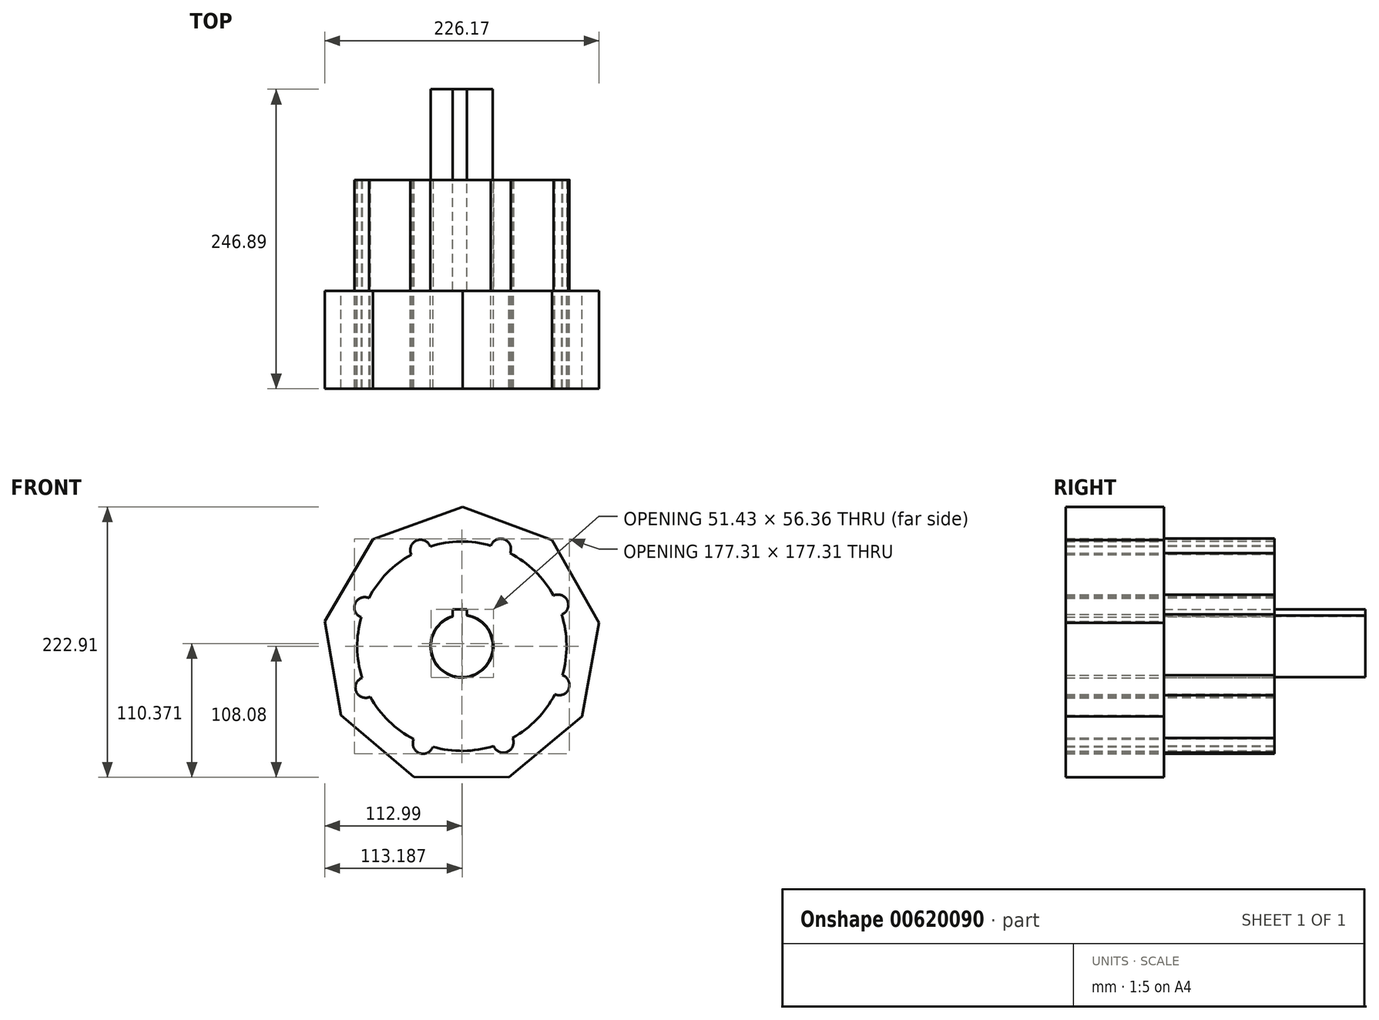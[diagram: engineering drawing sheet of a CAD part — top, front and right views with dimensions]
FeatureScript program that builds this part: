
annotation { "Feature Type Name" : "Feature", "Feature Type Description" : "" }
export const myFeature = defineFeature(function(context is Context, id is Id, definition is map)
    precondition{}
    {
        {
            var Q0;
            Q0=qCreatedBy(makeId("Front.planeOp"),FACE);
            var sketch = newSketch(context, id + "F0", { "sketchPlane" : qUnion([Q0])});
            skCircle(sketch, "E0.cCircle", {"center": v(-20.28, 0) * mm, "radius": 107.9 * mm, "construction": true});
            skLineSegment(sketch, "E0.0", {"start": v(92.9, 19.42) * mm, "end": v(78.9, -57.87) * mm});
            skLineSegment(sketch, "E0.1", {"start": v(78.9, -57.87) * mm, "end": v(18.5, -108.08) * mm});
            skLineSegment(sketch, "E0.2", {"start": v(18.5, -108.08) * mm, "end": v(-60.05, -107.72) * mm});
            skLineSegment(sketch, "E0.3", {"start": v(-60.05, -107.72) * mm, "end": v(-119.99, -56.96) * mm});
            skLineSegment(sketch, "E0.4", {"start": v(-119.99, -56.96) * mm, "end": v(-133.27, 20.46) * mm});
            skLineSegment(sketch, "E0.5", {"start": v(-133.27, 20.46) * mm, "end": v(-93.69, 88.3) * mm});
            skLineSegment(sketch, "E0.6", {"start": v(-93.69, 88.3) * mm, "end": v(-19.75, 114.83) * mm});
            skLineSegment(sketch, "E0.7", {"start": v(-19.75, 114.83) * mm, "end": v(53.93, 87.63) * mm});
            skLineSegment(sketch, "E0.8", {"start": v(53.93, 87.63) * mm, "end": v(92.9, 19.42) * mm});
            skPoint(sketch, "E0.0.midPoint", {"position": v(85.9, -19.22) * mm});
            skArc(sketch, "E1", {"start": v(-61.99, 75.56) * mm, "mid": v(-82.1, 60.21) * mm, "end": v(-96.91, 39.7) * mm});
            skArc(sketch, "E2", {"start": v(19.42, 76.63) * mm, "mid": v(14.84, 88.06) * mm, "end": v(3.65, 82.92) * mm});
            skArc(sketch, "E3.1.0", {"start": v(-46.4, 82.26) * mm, "mid": v(-57.71, 87.1) * mm, "end": v(-61.99, 75.56) * mm});
            skArc(sketch, "E3.2.0", {"start": v(-96.91, 39.7) * mm, "mid": v(-108.33, 35.12) * mm, "end": v(-103.2, 23.93) * mm});
            skArc(sketch, "E3.3.0", {"start": v(-102.54, -26.12) * mm, "mid": v(-107.38, -37.43) * mm, "end": v(-95.84, -41.7) * mm});
            skArc(sketch, "E3.4.0", {"start": v(-59.98, -76.63) * mm, "mid": v(-55.4, -88.06) * mm, "end": v(-44.21, -82.92) * mm});
            skArc(sketch, "E3.5.0", {"start": v(5.84, -82.26) * mm, "mid": v(17.15, -87.1) * mm, "end": v(21.43, -75.56) * mm});
            skArc(sketch, "E3.6.0", {"start": v(56.35, -39.7) * mm, "mid": v(67.78, -35.12) * mm, "end": v(62.64, -23.93) * mm});
            skArc(sketch, "E3.7.0", {"start": v(61.98, 26.12) * mm, "mid": v(66.82, 37.43) * mm, "end": v(55.28, 41.7) * mm});
            skArc(sketch, "E4.trimOffspring", {"start": v(-103.2, 23.93) * mm, "mid": v(-106.58, -1.14) * mm, "end": v(-102.54, -26.12) * mm});
            skArc(sketch, "E5.trimOffspring", {"start": v(-95.84, -41.7) * mm, "mid": v(-80.5, -61.83) * mm, "end": v(-59.98, -76.63) * mm});
            skArc(sketch, "E6.trimOffspring", {"start": v(-44.21, -82.92) * mm, "mid": v(-19.14, -86.3) * mm, "end": v(5.84, -82.26) * mm});
            skArc(sketch, "E7.trimOffspring", {"start": v(3.65, 82.92) * mm, "mid": v(-21.42, 86.3) * mm, "end": v(-46.4, 82.26) * mm});
            skArc(sketch, "E8.trimOffspring", {"start": v(21.43, -75.56) * mm, "mid": v(41.55, -60.21) * mm, "end": v(56.35, -39.7) * mm});
            skArc(sketch, "E9.trimOffspring", {"start": v(62.64, -23.93) * mm, "mid": v(66.02, 1.14) * mm, "end": v(61.98, 26.12) * mm});
            skArc(sketch, "E10.trimOffspring", {"start": v(55.28, 41.7) * mm, "mid": v(39.93, 61.83) * mm, "end": v(19.42, 76.63) * mm});
            skSolve(sketch);
        }
        {
            var Q0;
            Q0=makeQuery(id+"F0.imprint","IMPRINT",FACE,{"disambiguationData":[TD([[makeQuery(id+"F0.imprint","IMPRINT",EDGE,{"derivedFrom":sQuery(id+"F0.wireOp",EDGE,"E0.0")}),-1.0]])]});
            extrude(context, id + "F1", {"entities" : qUnion([Q0]), "depth" : 80.77 * mm, "offsetDistance" : 25.4 * mm});
        }
        {
            var Q0;
            Q0=makeQuery(id+"F1.opExtrude","CAP_FACE",FACE,{"disambiguationData":[OSD([sQuery(id+"F0.wireOp",EDGE,"E0.0"),sQuery(id+"F0.wireOp",EDGE,"E0.1"),sQuery(id+"F0.wireOp",EDGE,"E0.2"),sQuery(id+"F0.wireOp",EDGE,"E0.3"),sQuery(id+"F0.wireOp",EDGE,"E0.4"),sQuery(id+"F0.wireOp",EDGE,"E0.5"),sQuery(id+"F0.wireOp",EDGE,"E0.6"),sQuery(id+"F0.wireOp",EDGE,"E0.7"),sQuery(id+"F0.wireOp",EDGE,"E0.8"),sQuery(id+"F0.wireOp",EDGE,"E1"),sQuery(id+"F0.wireOp",EDGE,"E2"),sQuery(id+"F0.wireOp",EDGE,"E3.1.0"),sQuery(id+"F0.wireOp",EDGE,"E3.2.0"),sQuery(id+"F0.wireOp",EDGE,"E3.3.0"),sQuery(id+"F0.wireOp",EDGE,"E3.4.0"),sQuery(id+"F0.wireOp",EDGE,"E3.5.0"),sQuery(id+"F0.wireOp",EDGE,"E3.6.0"),sQuery(id+"F0.wireOp",EDGE,"E3.7.0"),sQuery(id+"F0.wireOp",EDGE,"E4.trimOffspring"),sQuery(id+"F0.wireOp",EDGE,"E5.trimOffspring"),sQuery(id+"F0.wireOp",EDGE,"E6.trimOffspring"),sQuery(id+"F0.wireOp",EDGE,"E7.trimOffspring"),sQuery(id+"F0.wireOp",EDGE,"E8.trimOffspring"),sQuery(id+"F0.wireOp",EDGE,"E9.trimOffspring"),sQuery(id+"F0.wireOp",EDGE,"E10.trimOffspring")])],"isStart":true});
            var sketch = newSketch(context, id + "F2", { "sketchPlane" : qUnion([Q0])});
            skArc(sketch, "E11", {"start": v(-4.4, 82.48) * mm, "mid": v(-14.52, 87.26) * mm, "end": v(-18.57, 76.83) * mm});
            skArc(sketch, "E12.0", {"start": v(-3.65, 82.92) * mm, "mid": v(21.42, 86.3) * mm, "end": v(46.4, 82.26) * mm});
            skArc(sketch, "E13", {"start": v(-18.57, 76.83) * mm, "mid": v(-39.79, 61.68) * mm, "end": v(-55.5, 40.87) * mm});
            skArc(sketch, "E14.1.0", {"start": v(-55.5, 40.87) * mm, "mid": v(-66.03, 37.1) * mm, "end": v(-61.52, 26.86) * mm});
            skArc(sketch, "E14.2.0", {"start": v(-62.2, -24.69) * mm, "mid": v(-66.98, -34.8) * mm, "end": v(-56.55, -38.85) * mm});
            skArc(sketch, "E14.3.0", {"start": v(-20.59, -75.78) * mm, "mid": v(-16.82, -86.31) * mm, "end": v(-6.58, -81.8) * mm});
            skArc(sketch, "E14.4.0", {"start": v(44.97, -82.48) * mm, "mid": v(55.08, -87.26) * mm, "end": v(59.13, -76.83) * mm});
            skArc(sketch, "E14.5.0", {"start": v(96.06, -40.87) * mm, "mid": v(106.6, -37.1) * mm, "end": v(102.08, -26.86) * mm});
            skArc(sketch, "E14.6.0", {"start": v(102.76, 24.69) * mm, "mid": v(107.54, 34.8) * mm, "end": v(97.11, 38.85) * mm});
            skArc(sketch, "E14.7.0", {"start": v(61.15, 75.78) * mm, "mid": v(57.38, 86.31) * mm, "end": v(47.14, 81.8) * mm});
            skArc(sketch, "E15.trimOffspring", {"start": v(97.11, 38.85) * mm, "mid": v(81.96, 60.07) * mm, "end": v(61.15, 75.78) * mm});
            skArc(sketch, "E16.trimOffspring", {"start": v(59.13, -76.83) * mm, "mid": v(80.35, -61.68) * mm, "end": v(96.06, -40.87) * mm});
            skArc(sketch, "E17.trimOffspring", {"start": v(-6.58, -81.8) * mm, "mid": v(19.14, -86.09) * mm, "end": v(44.97, -82.48) * mm});
            skArc(sketch, "E18.trimOffspring", {"start": v(-56.55, -38.85) * mm, "mid": v(-41.4, -60.07) * mm, "end": v(-20.59, -75.78) * mm});
            skArc(sketch, "E19.trimOffspring", {"start": v(-61.52, 26.86) * mm, "mid": v(-65.8, 1.14) * mm, "end": v(-62.2, -24.69) * mm});
            skCircle(sketch, "E20", {"center": v(20.28, 0) * mm, "radius": 48.29 * mm});
            skSolve(sketch);
        }
        {
            var Q0;
            Q0 = qSketchRegion(id + "F2", true);
            var Q1;
            Q1=makeQuery(id+"F2.imprint","IMPRINT",FACE,{"disambiguationData":[TD([[makeQuery(id+"F2.imprint","IMPRINT",EDGE,{"derivedFrom":sQuery(id+"F2.wireOp",EDGE,"E12.0")}),-1.0]])]});
            extrude(context, id + "F3", {"entities" : qUnion([Q0, Q1]), "depth" : 91.44 * mm, "offsetDistance" : 25.4 * mm});
        }
        {
            var Q0;
            Q0=makeQuery(id+"F3.opExtrude","CAP_FACE",FACE,{"disambiguationData":[OSD([sQuery(id+"F0.wireOp",EDGE,"E1"),sQuery(id+"F0.wireOp",EDGE,"E2"),sQuery(id+"F0.wireOp",EDGE,"E3.1.0"),sQuery(id+"F0.wireOp",EDGE,"E3.2.0"),sQuery(id+"F0.wireOp",EDGE,"E3.3.0"),sQuery(id+"F0.wireOp",EDGE,"E3.4.0"),sQuery(id+"F0.wireOp",EDGE,"E3.5.0"),sQuery(id+"F0.wireOp",EDGE,"E3.6.0"),sQuery(id+"F0.wireOp",EDGE,"E3.7.0"),sQuery(id+"F0.wireOp",EDGE,"E4.trimOffspring"),sQuery(id+"F0.wireOp",EDGE,"E5.trimOffspring"),sQuery(id+"F0.wireOp",EDGE,"E6.trimOffspring"),sQuery(id+"F0.wireOp",EDGE,"E8.trimOffspring"),sQuery(id+"F0.wireOp",EDGE,"E9.trimOffspring"),sQuery(id+"F0.wireOp",EDGE,"E10.trimOffspring"),sQuery(id+"F2.wireOp",EDGE,"E12.0")])],"isStart":false});
            var sketch = newSketch(context, id + "F4", { "sketchPlane" : qUnion([Q0])});
            skArc(sketch, "E21", {"start": v(16, 25.6) * mm, "mid": v(18.57, -25.9) * mm, "end": v(27.87, 24.81) * mm});
            skLineSegment(sketch, "E22.bottom", {"start": v(16, 30.47) * mm, "end": v(27.87, 30.47) * mm});
            skLineSegment(sketch, "E22.left", {"start": v(16, 30.47) * mm, "end": v(16, 25.6) * mm});
            skLineSegment(sketch, "E22.right", {"start": v(27.87, 30.47) * mm, "end": v(27.87, 24.81) * mm});
            skSolve(sketch);
        }
        {
            var Q0;
            Q0=makeQuery(id+"F4.imprint","IMPRINT",FACE,{"disambiguationData":[TD([[makeQuery(id+"F4.imprint","IMPRINT",EDGE,{"derivedFrom":sQuery(id+"F4.wireOp",EDGE,"E21")}),1.0]])]});
            extrude(context, id + "F5", {"entities" : qUnion([Q0]), "operationType" : NewBodyOperationType.REMOVE, "oppositeDirection" : true, "depth" : 218.7 * mm, "offsetDistance" : 25.4 * mm});
        }
        {
            var Q0;
            Q0=makeQuery(id+"F3.opExtrude","CAP_FACE",FACE,{"disambiguationData":[OSD([sQuery(id+"F0.wireOp",EDGE,"E1"),sQuery(id+"F0.wireOp",EDGE,"E2"),sQuery(id+"F0.wireOp",EDGE,"E3.1.0"),sQuery(id+"F0.wireOp",EDGE,"E3.2.0"),sQuery(id+"F0.wireOp",EDGE,"E3.3.0"),sQuery(id+"F0.wireOp",EDGE,"E3.4.0"),sQuery(id+"F0.wireOp",EDGE,"E3.5.0"),sQuery(id+"F0.wireOp",EDGE,"E3.6.0"),sQuery(id+"F0.wireOp",EDGE,"E3.7.0"),sQuery(id+"F0.wireOp",EDGE,"E4.trimOffspring"),sQuery(id+"F0.wireOp",EDGE,"E5.trimOffspring"),sQuery(id+"F0.wireOp",EDGE,"E6.trimOffspring"),sQuery(id+"F0.wireOp",EDGE,"E8.trimOffspring"),sQuery(id+"F0.wireOp",EDGE,"E9.trimOffspring"),sQuery(id+"F0.wireOp",EDGE,"E10.trimOffspring"),sQuery(id+"F2.wireOp",EDGE,"E12.0")])],"isStart":false});
            var sketch = newSketch(context, id + "F6", { "sketchPlane" : qUnion([Q0])});
            skArc(sketch, "E23", {"start": v(16, 25.2) * mm, "mid": v(18.57, -25.5) * mm, "end": v(27.87, 24.4) * mm});
            skLineSegment(sketch, "E24.top", {"start": v(16, 30.47) * mm, "end": v(27.87, 30.47) * mm});
            skLineSegment(sketch, "E24.left", {"start": v(16, 25.2) * mm, "end": v(16, 30.47) * mm});
            skLineSegment(sketch, "E24.right", {"start": v(27.87, 24.4) * mm, "end": v(27.87, 30.47) * mm});
            skSolve(sketch);
        }
        {
            var Q0;
            Q0 = qSketchRegion(id + "F6", true);
            extrude(context, id + "F7", {"entities" : qUnion([Q0]), "depth" : 74.68 * mm, "offsetDistance" : 25.4 * mm});
        }
        {
            var Q0;
            Q0=makeQuery(id+"F3.opExtrude","CAP_FACE",FACE,{"disambiguationData":[OSD([sQuery(id+"F0.wireOp",EDGE,"E1"),sQuery(id+"F0.wireOp",EDGE,"E2"),sQuery(id+"F0.wireOp",EDGE,"E3.1.0"),sQuery(id+"F0.wireOp",EDGE,"E3.2.0"),sQuery(id+"F0.wireOp",EDGE,"E3.3.0"),sQuery(id+"F0.wireOp",EDGE,"E3.4.0"),sQuery(id+"F0.wireOp",EDGE,"E3.5.0"),sQuery(id+"F0.wireOp",EDGE,"E3.6.0"),sQuery(id+"F0.wireOp",EDGE,"E3.7.0"),sQuery(id+"F0.wireOp",EDGE,"E4.trimOffspring"),sQuery(id+"F0.wireOp",EDGE,"E5.trimOffspring"),sQuery(id+"F0.wireOp",EDGE,"E6.trimOffspring"),sQuery(id+"F0.wireOp",EDGE,"E8.trimOffspring"),sQuery(id+"F0.wireOp",EDGE,"E9.trimOffspring"),sQuery(id+"F0.wireOp",EDGE,"E10.trimOffspring"),sQuery(id+"F2.wireOp",EDGE,"E12.0")])],"isStart":false});
            extrude(context, id + "F8", {"entities" : qUnion([Q0]), "operationType" : NewBodyOperationType.ADD, "oppositeDirection" : true, "depth" : 15.5 * mm, "offsetDistance" : 25.4 * mm});
        }
    });
